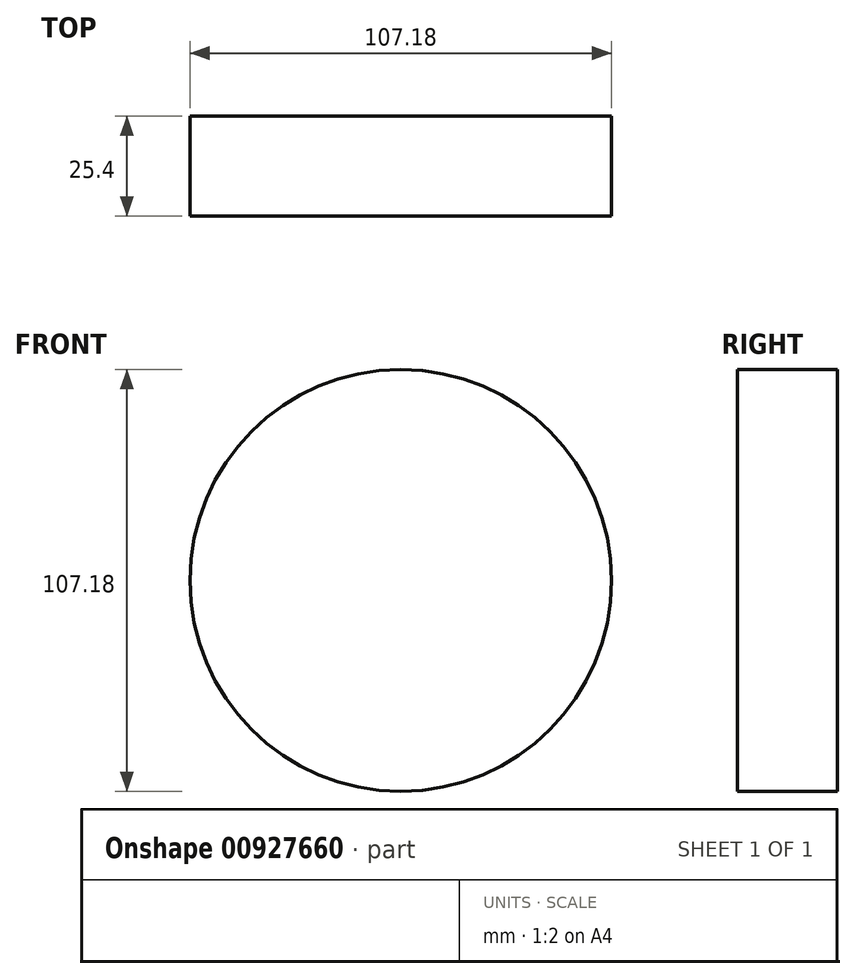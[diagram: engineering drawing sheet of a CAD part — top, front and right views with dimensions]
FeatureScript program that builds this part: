
annotation { "Feature Type Name" : "Feature", "Feature Type Description" : "" }
export const myFeature = defineFeature(function(context is Context, id is Id, definition is map)
    precondition{}
    {
        {
            var Q0;
            Q0=qCreatedBy(makeId("Front.planeOp"),FACE);
            var sketch = newSketch(context, id + "F0", { "sketchPlane" : qUnion([Q0])});
            skCircle(sketch, "E0", {"center": v(0, 0) * mm, "radius": 53.59 * mm});
            skSolve(sketch);
        }
        {
            var Q0;
            Q0 = qSketchRegion(id + "F0", true);
            extrude(context, id + "F1", {"entities" : qUnion([Q0]), "depth" : 25.4 * mm, "offsetDistance" : 25.4 * mm});
        }
    });
